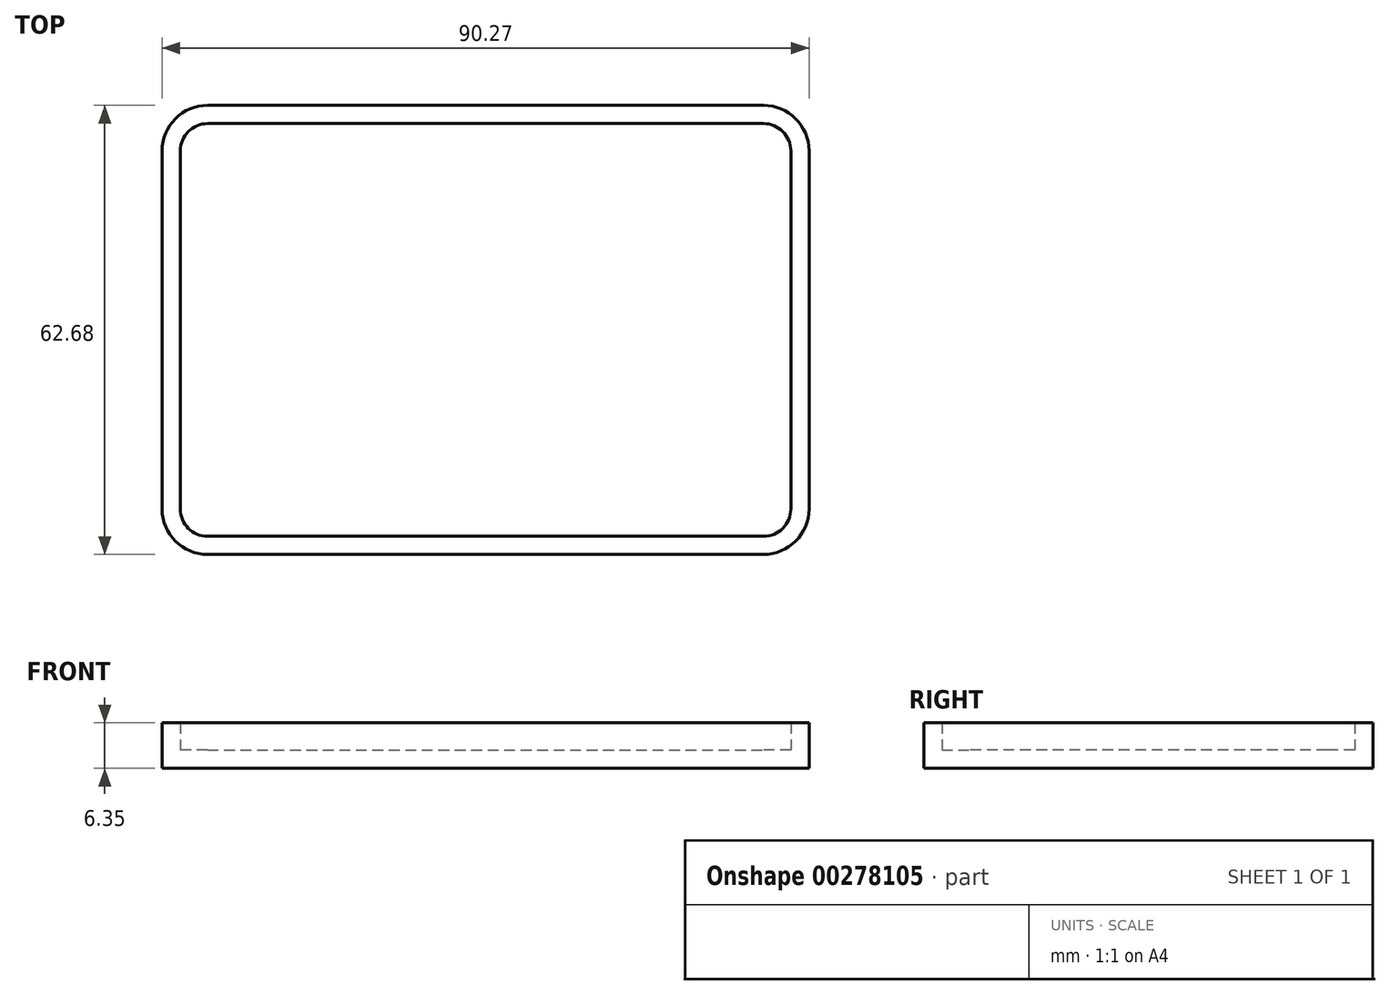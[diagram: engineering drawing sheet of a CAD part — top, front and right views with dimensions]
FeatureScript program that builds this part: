
annotation { "Feature Type Name" : "Feature", "Feature Type Description" : "" }
export const myFeature = defineFeature(function(context is Context, id is Id, definition is map)
    precondition{}
    {
        {
            var Q0;
            Q0=qCreatedBy(makeId("Top.planeOp"),FACE);
            var sketch = newSketch(context, id + "F0", { "sketchPlane" : qUnion([Q0])});
            skLineSegment(sketch, "E0.bottom", {"start": v(-39.38, 42.92) * mm, "end": v(38.2, 42.92) * mm});
            skLineSegment(sketch, "E0.top", {"start": v(-39.38, -19.76) * mm, "end": v(38.2, -19.76) * mm});
            skLineSegment(sketch, "E0.left", {"start": v(-45.73, 36.57) * mm, "end": v(-45.73, -13.4) * mm});
            skLineSegment(sketch, "E0.right", {"start": v(44.54, 36.57) * mm, "end": v(44.54, -13.4) * mm});
            skPoint(sketch, "E1.visualSharp", {"position": v(-45.73, 42.92) * mm});
            skArc(sketch, "E1.filletArc", {"start": v(-39.38, 42.92) * mm, "mid": v(-43.87, 41.06) * mm, "end": v(-45.73, 36.57) * mm});
            skPoint(sketch, "E2.visualSharp", {"position": v(44.54, 42.92) * mm});
            skArc(sketch, "E2.filletArc", {"start": v(44.54, 36.57) * mm, "mid": v(42.68, 41.06) * mm, "end": v(38.2, 42.92) * mm});
            skPoint(sketch, "E3.visualSharp", {"position": v(-45.73, -19.76) * mm});
            skArc(sketch, "E3.filletArc", {"start": v(-45.73, -13.4) * mm, "mid": v(-43.87, -17.9) * mm, "end": v(-39.38, -19.76) * mm});
            skPoint(sketch, "E4.visualSharp", {"position": v(44.54, -19.76) * mm});
            skArc(sketch, "E4.filletArc", {"start": v(38.2, -19.76) * mm, "mid": v(42.68, -17.9) * mm, "end": v(44.54, -13.4) * mm});
            skSolve(sketch);
        }
        {
            var Q0;
            Q0=makeQuery(id+"F0.imprint","IMPRINT",FACE,{"disambiguationData":[TD([[makeQuery(id+"F0.imprint","IMPRINT",EDGE,{"derivedFrom":sQuery(id+"F0.wireOp",EDGE,"E0.bottom")}),-1.0]])]});
            var sketch = newSketch(context, id + "F2", { "sketchPlane" : qUnion([Q0])});
            skArc(sketch, "E5.0", {"start": v(-39.38, 40.38) * mm, "mid": v(-42.07, 39.27) * mm, "end": v(-43.2, 36.57) * mm});
            skLineSegment(sketch, "E5.1", {"start": v(-39.38, 40.38) * mm, "end": v(38.2, 40.38) * mm});
            skLineSegment(sketch, "E5.2", {"start": v(-43.2, 36.57) * mm, "end": v(-43.2, -13.4) * mm});
            skArc(sketch, "E5.3", {"start": v(42, 36.57) * mm, "mid": v(40.89, 39.27) * mm, "end": v(38.2, 40.38) * mm});
            skArc(sketch, "E5.4", {"start": v(-43.2, -13.4) * mm, "mid": v(-42.07, -16.1) * mm, "end": v(-39.38, -17.22) * mm});
            skLineSegment(sketch, "E5.5", {"start": v(-39.38, -17.22) * mm, "end": v(38.2, -17.22) * mm});
            skArc(sketch, "E5.6", {"start": v(38.2, -17.22) * mm, "mid": v(40.89, -16.1) * mm, "end": v(42, -13.4) * mm});
            skLineSegment(sketch, "E5.7", {"start": v(42, 36.57) * mm, "end": v(42, -13.4) * mm});
            skSolve(sketch);
        }
        {
            var Q0;
            Q0=makeQuery(id+"F2.imprint","IMPRINT",FACE,{"disambiguationData":[TD([[makeQuery(id+"F2.imprint","IMPRINT",EDGE,{"derivedFrom":sQuery(id+"F2.wireOp",EDGE,"E5.0")}),-1.0]])]});
            extrude(context, id + "F3", {"entities" : qUnion([Q0]), "depth" : 6.35 * mm});
        }
        {
            var Q0;
            Q0=makeQuery(id+"F0.imprint","IMPRINT",FACE,{"disambiguationData":[TD([[makeQuery(id+"F0.imprint","IMPRINT",EDGE,{"derivedFrom":sQuery(id+"F0.wireOp",EDGE,"E0.bottom")}),-1.0]])]});
            extrude(context, id + "F1", {"entities" : qUnion([Q0]), "operationType" : NewBodyOperationType.ADD, "depth" : 2.54 * mm});
        }
    });
